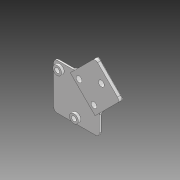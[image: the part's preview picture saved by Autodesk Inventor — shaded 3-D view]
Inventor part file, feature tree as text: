
AUTODESK INVENTOR PART (.ipt)
format: ipt  version: 2020 (Build 240168000, 168)  size: 386,048 bytes
history: native  units: mm
features: sketch x8, extrude x8, plane x2, fillet x2, projected_geometry x2, mirror x1
ambient origin geometry x8: Origin, YZ Plane, XZ Plane, XY Plane, X Axis, Y Axis, Z Axis, Center Point
bodies: Solid1 (feature_tree)
feature tree (23):
  sketch  "Sketch1"  dims[d0=26.0mm d1=26.0mm]
  extrude  "Extrusion1"  Depth=26.0mm
  plane  "Work Plane1"
  sketch  "Sketch3"  dims[d5=1.0mm d6=0.0mm d7=2.0mm]
  extrude  "Extrusion3"  Depth=2.7mm
  extrude  "Extrusion8"  Depth=2.0mm
  extrude  "Extrusion5"  Depth=1.5mm TaperAngle=0.0deg
  extrude  "Extrusion2"  Depth=12.0mm
  plane  "Work Plane2"
  extrude  "Extrusion6"  Depth=3.0mm
  extrude  "Extrusion7"  Depth=25.0mm
  extrude  "Extrusion9"  Depth=15.0mm TaperAngle=0.0deg
  mirror  "Mirror1"
  fillet  "Fillet1"  Radius=3.0mm
  fillet  "Fillet2"  Radius=2.0mm
  sketch  "Sketch2"  dims[d3=19.0mm d4=2.7mm]
  sketch  "Sketch4"  dims[d8=5.0mm d9=1.5mm d10=0.0mm]
  projected_geometry  "Projected Loop1"
  sketch  "Sketch6"  dims[d11=25.0mm d12=12.0mm]
  sketch  "Sketch7"  dims[d13=2.0mm d14=3.0mm]
  projected_geometry  "Projected Loop2"
  sketch  "Sketch8"  dims[d15=10.0mm d16=25.0mm]
  sketch  "Sketch9"  dims[d17=20.0mm d18=0.0mm d22=15.0mm d23=0.0mm d24=3.0mm d25=2.0mm d26=-3.0mm d29=4.0mm d30=4.0mm d31=3.3mm d32=3.0mm d33=0.0mm d34=6.0mm d35=3.0mm d36=0.0mm d37=10.0mm d38=12.0mm d39=12.0mm d40=25.0mm d41=19.0mm d42=6.659mm d43=0.0mm d44=12.0mm d45=12.0mm d46=4.0mm d47=1.5mm d48=0.0mm d49=10.0mm d50=10.0mm d51=5.0mm d52=1.5mm d53=0.5mm]
